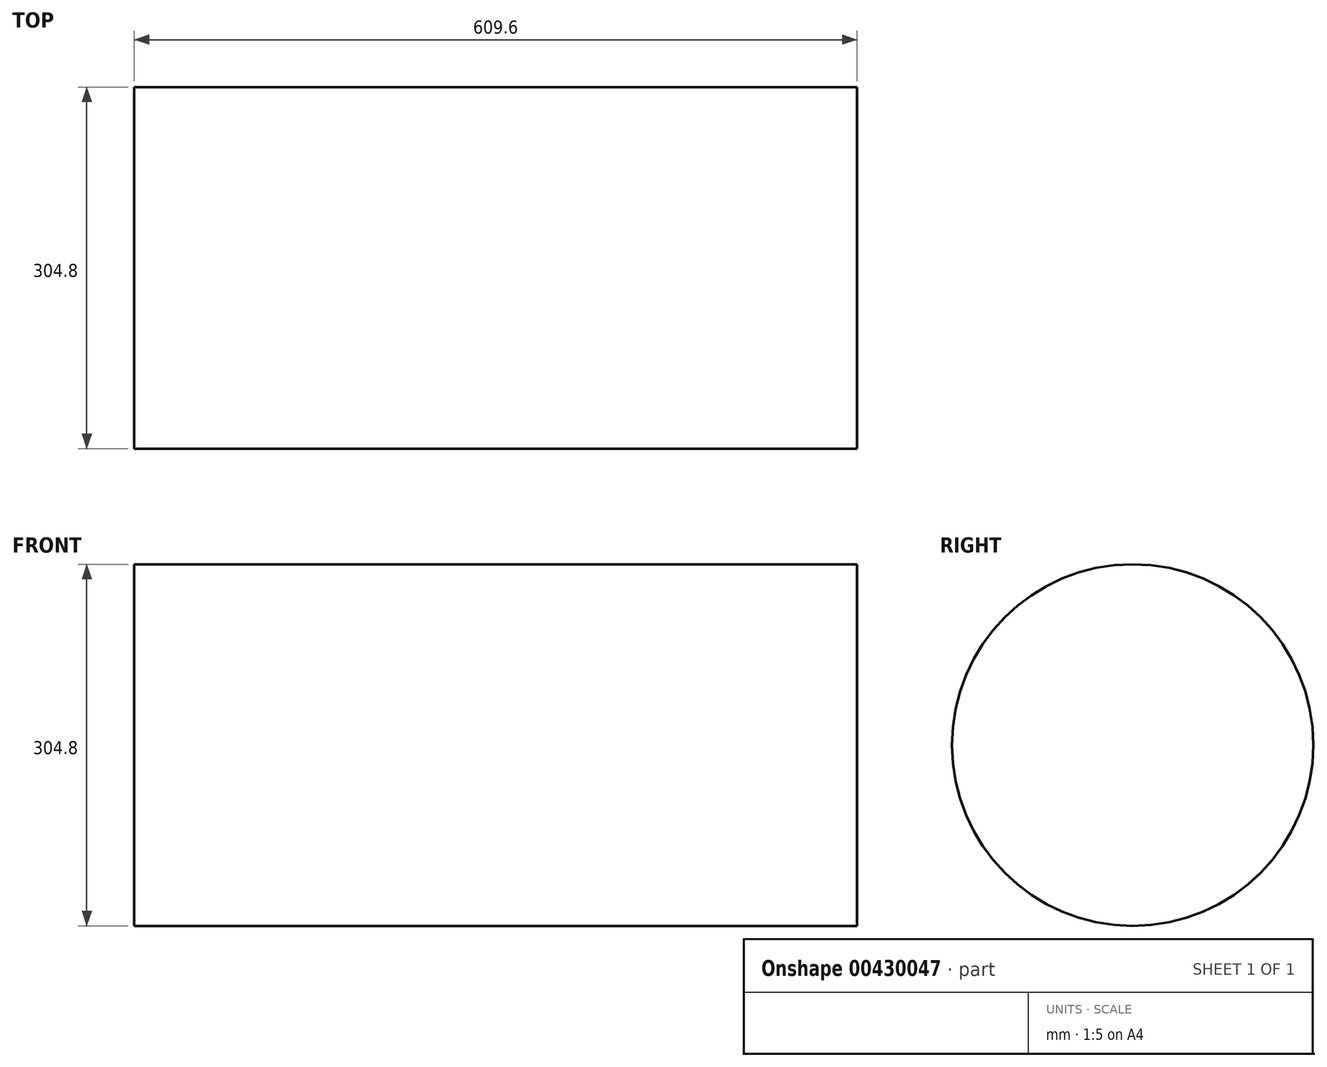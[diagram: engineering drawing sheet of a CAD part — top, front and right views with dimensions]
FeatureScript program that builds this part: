
annotation { "Feature Type Name" : "Feature", "Feature Type Description" : "" }
export const myFeature = defineFeature(function(context is Context, id is Id, definition is map)
    precondition{}
    {
        {
            var Q0;
            Q0=qCreatedBy(makeId("Right.planeOp"),FACE);
            var sketch = newSketch(context, id + "F0", { "sketchPlane" : qUnion([Q0])});
            skCircle(sketch, "E0", {"center": v(0, 0) * mm, "radius": 152.4 * mm});
            skSolve(sketch);
        }
        {
            var Q0;
            Q0 = qSketchRegion(id + "F0", true);
            extrude(context, id + "F1", {"entities" : qUnion([Q0]), "depth" : 609.6 * mm});
        }
    });
